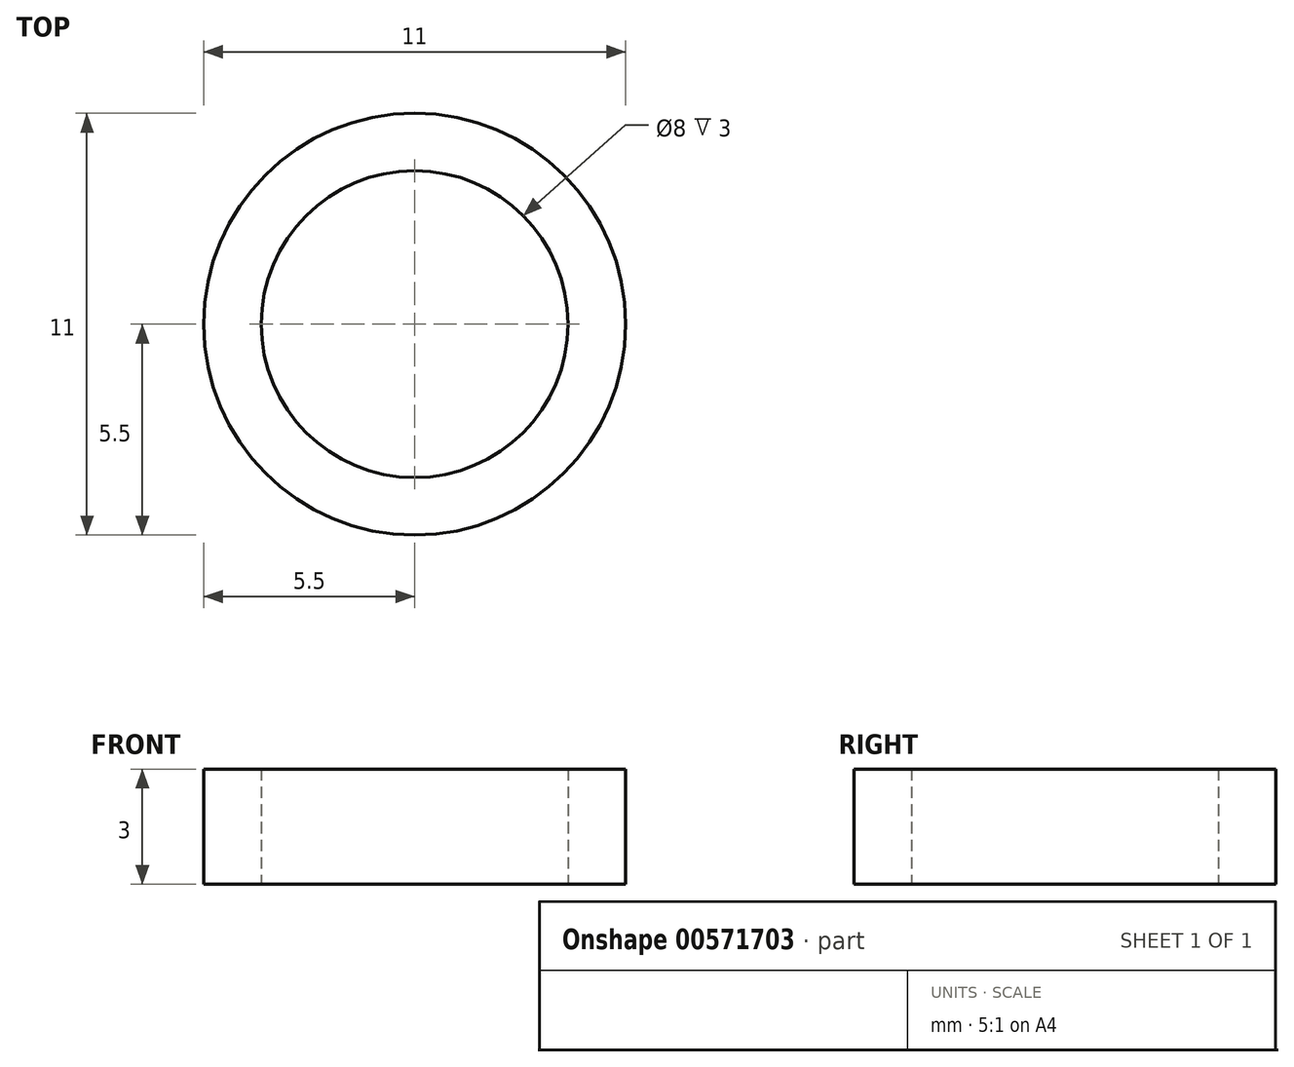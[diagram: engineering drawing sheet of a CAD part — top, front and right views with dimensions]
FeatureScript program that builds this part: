
annotation { "Feature Type Name" : "Feature", "Feature Type Description" : "" }
export const myFeature = defineFeature(function(context is Context, id is Id, definition is map)
    precondition{}
    {
        {
            var Q0;
            Q0=qCreatedBy(makeId("Top.planeOp"),FACE);
            var sketch = newSketch(context, id + "F0", { "sketchPlane" : qUnion([Q0])});
            skCircle(sketch, "E0", {"center": v(0, 0) * mm, "radius": 5.5 * mm});
            skCircle(sketch, "E1", {"center": v(0, 0) * mm, "radius": 4 * mm});
            skSolve(sketch);
        }
        {
            var Q0;
            Q0=makeQuery(id+"F0.imprint","IMPRINT",FACE,{"disambiguationData":[TD([[makeQuery(id+"F0.imprint","IMPRINT",EDGE,{"derivedFrom":sQuery(id+"F0.wireOp",EDGE,"E0")}),1.0]])]});
            extrude(context, id + "F1", {"entities" : qUnion([Q0]), "depth" : 3 * mm, "offsetDistance" : 25 * mm});
        }
    });
